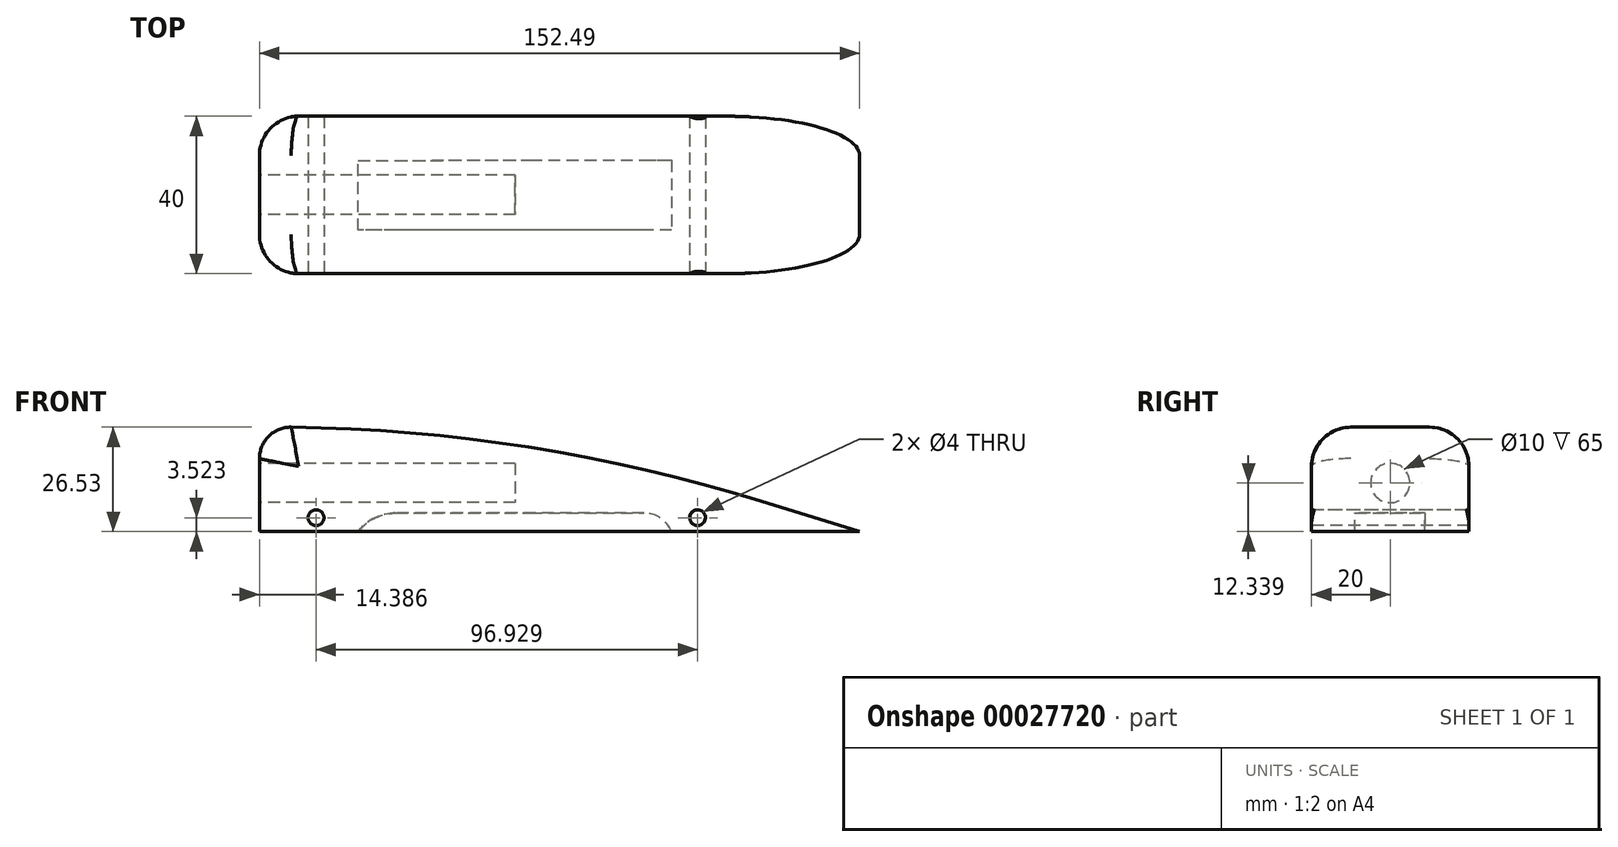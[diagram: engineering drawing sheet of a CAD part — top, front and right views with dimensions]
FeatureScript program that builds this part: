
annotation { "Feature Type Name" : "Feature", "Feature Type Description" : "" }
export const myFeature = defineFeature(function(context is Context, id is Id, definition is map)
    precondition{}
    {
        {
            var Q0;
            Q0=qCreatedBy(makeId("Front.planeOp"),FACE);
            var sketch = newSketch(context, id + "F0", { "sketchPlane" : qUnion([Q0])});
            skLineSegment(sketch, "E0.bottom", {"start": v(-84.2, -32.3) * mm, "end": v(215.8, -32.3) * mm});
            skLineSegment(sketch, "E0.top", {"start": v(-84.2, 37.7) * mm, "end": v(215.8, 37.7) * mm});
            skLineSegment(sketch, "E0.left", {"start": v(-84.2, -32.3) * mm, "end": v(-84.2, 37.7) * mm});
            skLineSegment(sketch, "E0.right", {"start": v(215.8, -32.3) * mm, "end": v(215.8, 37.7) * mm});
            skSolve(sketch);
        }
        {
            var Q0;
            Q0=makeQuery(id+"F0.imprint","IMPRINT",FACE,{"disambiguationData":[TD([[makeQuery(id+"F0.imprint","IMPRINT",EDGE,{"derivedFrom":sQuery(id+"F0.wireOp",EDGE,"E0.bottom")}),1.0]])]});
            extrude(context, id + "F1", {"entities" : qUnion([Q0]), "depth" : 40 * mm});
        }
        {
            var Q0;
            Q0=makeQuery(id+"F1.opExtrude","SWEPT_FACE",FACE,{"disambiguationData":[OSD([sQuery(id+"F0.wireOp",EDGE,"E0.left")])]});
            var sketch = newSketch(context, id + "F2", { "sketchPlane" : qUnion([Q0])});
            skCircle(sketch, "E1", {"center": v(20, -19.96) * mm, "radius": 5 * mm});
            skLineSegment(sketch, "E2", {"start": v(20, 37.7) * mm, "end": v(20, -32.3) * mm});
            skSolve(sketch);
        }
        {
            var Q0;
            Q0=makeQuery(id+"F2.imprint","IMPRINT",FACE,{"disambiguationData":[TD([[makeQuery(id+"F2.imprint","IMPRINT",EDGE,{"derivedFrom":sQuery(id+"F2.wireOp",EDGE,"E1")}),1.0]])]});
            extrude(context, id + "F3", {"entities" : qUnion([Q0]), "operationType" : NewBodyOperationType.REMOVE, "oppositeDirection" : true, "depth" : 65 * mm});
        }
        {
            var Q0;
            Q0=makeQuery(id+"F1.opExtrude","CAP_FACE",FACE,{"disambiguationData":[OSD([sQuery(id+"F0.wireOp",EDGE,"E0.bottom"),sQuery(id+"F0.wireOp",EDGE,"E0.top"),sQuery(id+"F0.wireOp",EDGE,"E0.left"),sQuery(id+"F0.wireOp",EDGE,"E0.right")])],"isStart":false});
            var sketch = newSketch(context, id + "F4", { "sketchPlane" : qUnion([Q0])});
            skCircle(sketch, "E3", {"center": v(-69.81, -28.78) * mm, "radius": 2 * mm});
            skCircle(sketch, "E4", {"center": v(27.11, -28.78) * mm, "radius": 2 * mm});
            skLineSegment(sketch, "E5", {"start": v(-36.14, 0) * mm, "end": v(68.3, -32.3) * mm});
            skLineSegment(sketch, "E6", {"start": v(-36.14, 0) * mm, "end": v(-84.2, -5.75) * mm});
            skSolve(sketch);
        }
        {
            var Q0;
            Q0=makeQuery(id+"F4.imprint","IMPRINT",FACE,{"disambiguationData":[TD([[makeQuery(id+"F4.imprint","IMPRINT",EDGE,{"derivedFrom":sQuery(id+"F4.wireOp",EDGE,"E3")}),1.0]])]});
            var Q1;
            Q1=makeQuery(id+"F4.imprint","IMPRINT",FACE,{"disambiguationData":[TD([[makeQuery(id+"F4.imprint","IMPRINT",EDGE,{"derivedFrom":sQuery(id+"F4.wireOp",EDGE,"E4")}),1.0]])]});
            extrude(context, id + "F5", {"entities" : qUnion([Q0, Q1]), "operationType" : NewBodyOperationType.REMOVE, "endBound" : BoundingType.THROUGH_ALL, "oppositeDirection" : true, "depth" : 25 * mm});
        }
        {
            var Q0;
            Q0 = qSketchRegion(id + "F4", true);
            var Q1;
            {var subQ4=sQuery(id+"F4.wireOp",EDGE,"E5");Q1=makeQuery(id+"F4.imprint","IMPRINT",FACE,{"disambiguationData":[TD([[makeQuery(id+"F4.imprint","IMPRINT",EDGE,{"derivedFrom":subQ4}),1.0]])]});}
            extrude(context, id + "F6", {"entities" : qUnion([Q0, Q1]), "operationType" : NewBodyOperationType.REMOVE, "endBound" : BoundingType.THROUGH_ALL, "oppositeDirection" : true, "depth" : 25 * mm});
        }
        {
            var Q0;
            Q0=makeQuery(id+"F6.boolean.opBoolean","COPY",EDGE,{"derivedFrom":makeQuery(id+"F6.opExtrude","SWEPT_EDGE",EDGE,{"disambiguationData":[OSD([sQuery(id+"F4.wireOp",EDGE,"E5"),sQuery(id+"F4.wireOp",EDGE,"E6")])]})});
            fillet(context, id + "F7", {"entities" : qUnion([Q0]), "radius" : 420.15 * mm, "tangentPropagation" : true, "allowEdgeOverflow" : false});
        }
        {
            var Q0;
            Q0=makeQuery(id+"F7.opFillet","BLEND_EDGE",EDGE,{"blendedFrom":[makeQuery(id+"F6.boolean.opBoolean","COPY",EDGE,{"derivedFrom":makeQuery(id+"F6.opExtrude","SWEPT_EDGE",EDGE,{"disambiguationData":[OSD([sQuery(id+"F4.wireOp",EDGE,"E5"),sQuery(id+"F4.wireOp",EDGE,"E6")])]})}),makeQuery(id+"F1.opExtrude","SWEPT_FACE",FACE,{"disambiguationData":[OSD([sQuery(id+"F0.wireOp",EDGE,"E0.left")])]})],"blendedInto":[makeQuery(id+"F1.opExtrude","SWEPT_FACE",FACE,{"disambiguationData":[OSD([sQuery(id+"F0.wireOp",EDGE,"E0.left")])]})]});
            fillet(context, id + "F8", {"entities" : qUnion([Q0]), "radius" : 8 * mm, "tangentPropagation" : true, "allowEdgeOverflow" : false});
        }
        {
            var Q0;
            Q0=makeQuery(id+"F7.opFillet","BLEND_EDGE",EDGE,{"blendedFrom":[makeQuery(id+"F6.boolean.opBoolean","COPY",EDGE,{"derivedFrom":makeQuery(id+"F6.opExtrude","SWEPT_EDGE",EDGE,{"disambiguationData":[OSD([sQuery(id+"F4.wireOp",EDGE,"E5"),sQuery(id+"F4.wireOp",EDGE,"E6")])]})}),makeQuery(id+"F1.opExtrude","CAP_FACE",FACE,{"disambiguationData":[OSD([sQuery(id+"F0.wireOp",EDGE,"E0.bottom"),sQuery(id+"F0.wireOp",EDGE,"E0.top"),sQuery(id+"F0.wireOp",EDGE,"E0.left"),sQuery(id+"F0.wireOp",EDGE,"E0.right")])],"isStart":false})],"blendedInto":[makeQuery(id+"F1.opExtrude","CAP_FACE",FACE,{"disambiguationData":[OSD([sQuery(id+"F0.wireOp",EDGE,"E0.bottom"),sQuery(id+"F0.wireOp",EDGE,"E0.top"),sQuery(id+"F0.wireOp",EDGE,"E0.left"),sQuery(id+"F0.wireOp",EDGE,"E0.right")])],"isStart":false})]});
            var Q1;
            Q1=makeQuery(id+"F7.opFillet","BLEND_EDGE",EDGE,{"blendedFrom":[makeQuery(id+"F6.boolean.opBoolean","COPY",EDGE,{"derivedFrom":makeQuery(id+"F6.opExtrude","SWEPT_EDGE",EDGE,{"disambiguationData":[OSD([sQuery(id+"F4.wireOp",EDGE,"E5"),sQuery(id+"F4.wireOp",EDGE,"E6")])]})}),makeQuery(id+"F1.opExtrude","CAP_FACE",FACE,{"disambiguationData":[OSD([sQuery(id+"F0.wireOp",EDGE,"E0.bottom"),sQuery(id+"F0.wireOp",EDGE,"E0.top"),sQuery(id+"F0.wireOp",EDGE,"E0.left"),sQuery(id+"F0.wireOp",EDGE,"E0.right")])],"isStart":true})],"blendedInto":[makeQuery(id+"F1.opExtrude","CAP_FACE",FACE,{"disambiguationData":[OSD([sQuery(id+"F0.wireOp",EDGE,"E0.bottom"),sQuery(id+"F0.wireOp",EDGE,"E0.top"),sQuery(id+"F0.wireOp",EDGE,"E0.left"),sQuery(id+"F0.wireOp",EDGE,"E0.right")])],"isStart":true})]});
            fillet(context, id + "F9", {"entities" : qUnion([Q0, Q1]), "radius" : 10 * mm, "tangentPropagation" : true, "allowEdgeOverflow" : false});
        }
        {
            var Q0;
            Q0=makeQuery(id+"F1.opExtrude","SWEPT_FACE",FACE,{"disambiguationData":[OSD([sQuery(id+"F0.wireOp",EDGE,"E0.bottom")])]});
            var sketch = newSketch(context, id + "F10", { "sketchPlane" : qUnion([Q0])});
            skLineSegment(sketch, "E7", {"start": v(-15.37, 11.18) * mm, "end": v(20.51, 11.18) * mm});
            skLineSegment(sketch, "E8", {"start": v(20.51, 11.18) * mm, "end": v(20.51, 28.97) * mm});
            skLineSegment(sketch, "E9", {"start": v(20.51, 28.97) * mm, "end": v(-15.37, 28.97) * mm});
            skLineSegment(sketch, "E10", {"start": v(-15.37, 28.97) * mm, "end": v(-59.1, 28.97) * mm});
            skLineSegment(sketch, "E11", {"start": v(-59.1, 28.97) * mm, "end": v(-59.1, 11.22) * mm});
            skLineSegment(sketch, "E12", {"start": v(-59.1, 11.22) * mm, "end": v(-15.37, 11.18) * mm});
            skSolve(sketch);
        }
        {
            var Q0;
            Q0=makeQuery(id+"F10.imprint","IMPRINT",FACE,{"disambiguationData":[TD([[makeQuery(id+"F10.imprint","IMPRINT",EDGE,{"derivedFrom":sQuery(id+"F10.wireOp",EDGE,"E7")}),1.0]])]});
            extrude(context, id + "F11", {"entities" : qUnion([Q0]), "operationType" : NewBodyOperationType.REMOVE, "oppositeDirection" : true, "depth" : 4.7 * mm});
        }
        {
            var Q0;
            Q0=makeQuery(id+"F11.boolean.opBoolean","COPY",EDGE,{"derivedFrom":makeQuery(id+"F11.opExtrude","CAP_EDGE",EDGE,{"disambiguationData":[OSD([sQuery(id+"F10.wireOp",EDGE,"E11")])],"isStart":false})});
            fillet(context, id + "F12", {"entities" : qUnion([Q0]), "radius" : 12 * mm, "tangentPropagation" : true, "allowEdgeOverflow" : false});
        }
        {
            var Q0;
            Q0=makeQuery(id+"F11.boolean.opBoolean","COPY",EDGE,{"derivedFrom":makeQuery(id+"F11.opExtrude","CAP_EDGE",EDGE,{"disambiguationData":[OSD([sQuery(id+"F10.wireOp",EDGE,"E8")])],"isStart":false})});
            fillet(context, id + "F13", {"entities" : qUnion([Q0]), "radius" : 7.5 * mm, "tangentPropagation" : true, "allowEdgeOverflow" : false});
        }
    });
